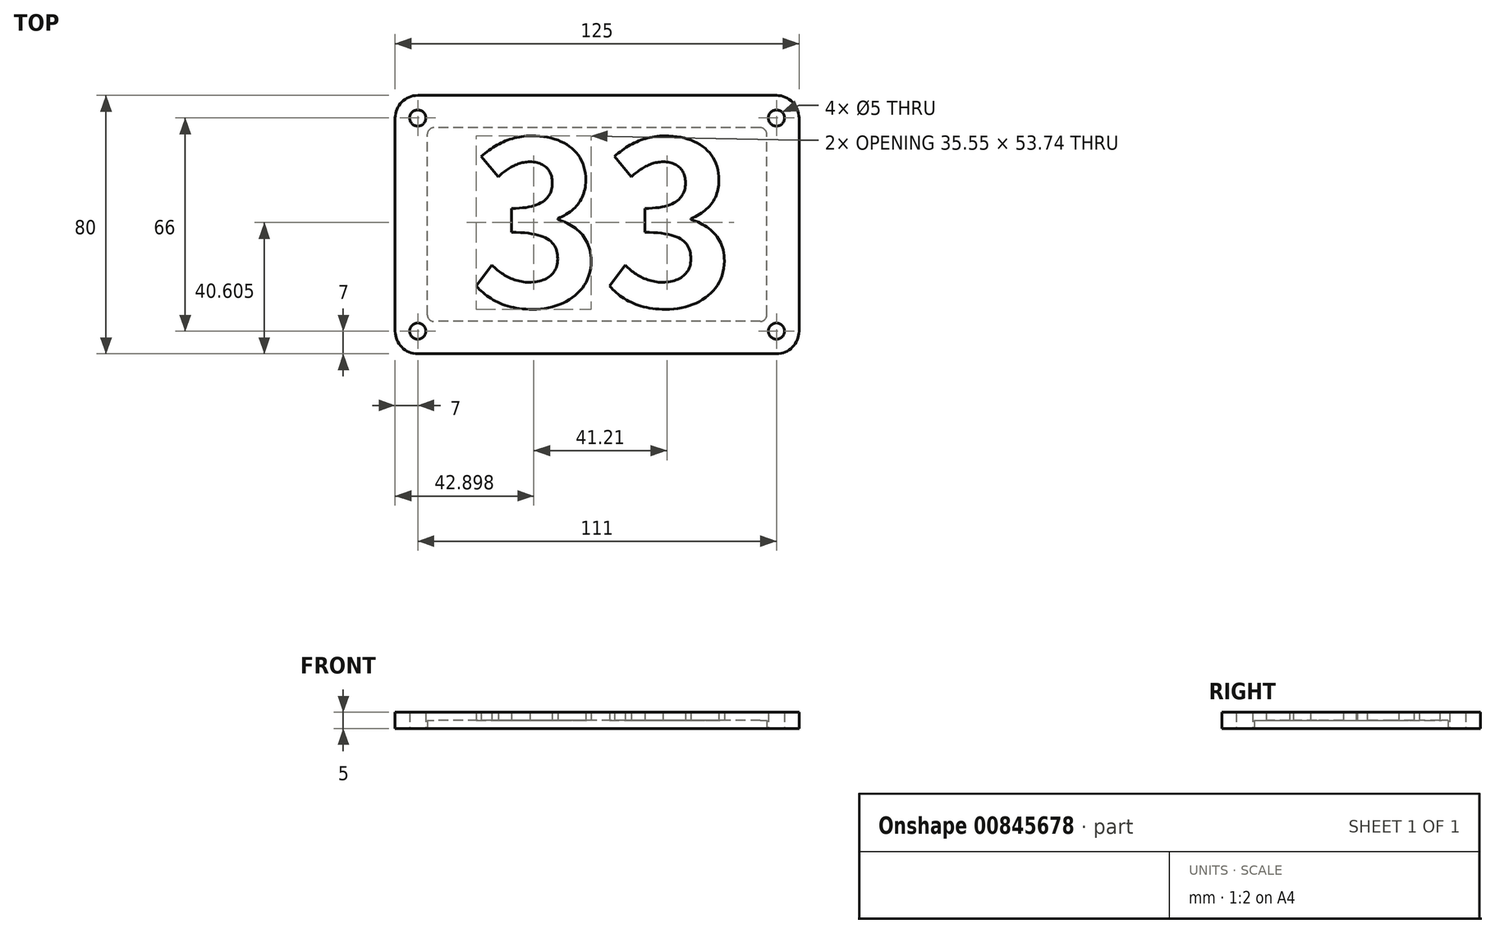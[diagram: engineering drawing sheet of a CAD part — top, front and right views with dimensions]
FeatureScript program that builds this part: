
annotation { "Feature Type Name" : "Feature", "Feature Type Description" : "" }
export const myFeature = defineFeature(function(context is Context, id is Id, definition is map)
    precondition{}
    {
        {
            var Q0;
            Q0=qCreatedBy(makeId("Top.planeOp"),FACE);
            var sketch = newSketch(context, id + "F0", { "sketchPlane" : qUnion([Q0])});
            skLineSegment(sketch, "E0.bottom", {"start": v(55.5, -40) * mm, "end": v(-55.5, -40) * mm});
            skLineSegment(sketch, "E0.top", {"start": v(55.5, 40) * mm, "end": v(-55.5, 40) * mm});
            skLineSegment(sketch, "E0.left", {"start": v(62.5, -33) * mm, "end": v(62.5, 33) * mm});
            skLineSegment(sketch, "E0.right", {"start": v(-62.5, -33) * mm, "end": v(-62.5, 33) * mm});
            skPoint(sketch, "E0.middle", {"position": v(0, 0) * mm});
            skPoint(sketch, "E1.visualSharp", {"position": v(-62.5, 40) * mm});
            skArc(sketch, "E1.filletArc", {"start": v(-55.5, 40) * mm, "mid": v(-60.45, 37.95) * mm, "end": v(-62.5, 33) * mm});
            skPoint(sketch, "E2.visualSharp", {"position": v(62.5, 40) * mm});
            skArc(sketch, "E2.filletArc", {"start": v(62.5, 33) * mm, "mid": v(60.45, 37.95) * mm, "end": v(55.5, 40) * mm});
            skPoint(sketch, "E3.visualSharp", {"position": v(62.5, -40) * mm});
            skArc(sketch, "E3.filletArc", {"start": v(55.5, -40) * mm, "mid": v(60.45, -37.95) * mm, "end": v(62.5, -33) * mm});
            skPoint(sketch, "E4.visualSharp", {"position": v(-62.5, -40) * mm});
            skArc(sketch, "E4.filletArc", {"start": v(-62.5, -33) * mm, "mid": v(-60.45, -37.95) * mm, "end": v(-55.5, -40) * mm});
            skCircle(sketch, "E5", {"center": v(55.5, 33) * mm, "radius": 2.5 * mm});
            skCircle(sketch, "E6", {"center": v(55.5, -33) * mm, "radius": 2.5 * mm});
            skCircle(sketch, "E7", {"center": v(-55.5, -33) * mm, "radius": 2.5 * mm});
            skCircle(sketch, "E8", {"center": v(-55.5, 33) * mm, "radius": 2.5 * mm});
            skSolve(sketch);
        }
        {
            var Q0;
            Q0=makeQuery(id+"F0.imprint","IMPRINT",FACE,{"disambiguationData":[TD([[makeQuery(id+"F0.imprint","IMPRINT",EDGE,{"derivedFrom":sQuery(id+"F0.wireOp",EDGE,"E0.bottom")}),-1.0]])]});
            extrude(context, id + "F1", {"entities" : qUnion([Q0]), "depth" : 5 * mm, "offsetDistance" : 25 * mm});
        }
        {
            var Q0;
            Q0=qCreatedBy(makeId("Top.planeOp"),FACE);
            var sketch = newSketch(context, id + "F2", { "sketchPlane" : qUnion([Q0])});
            skLineSegment(sketch, "E9.bottom", {"start": v(50.5, -30) * mm, "end": v(-50.5, -30) * mm});
            skLineSegment(sketch, "E9.top", {"start": v(50.5, 30) * mm, "end": v(-50.5, 30) * mm});
            skLineSegment(sketch, "E9.left", {"start": v(52.5, -28) * mm, "end": v(52.5, 28) * mm});
            skLineSegment(sketch, "E9.right", {"start": v(-52.5, -28) * mm, "end": v(-52.5, 28) * mm});
            skPoint(sketch, "E9.middle", {"position": v(0, 0) * mm});
            skPoint(sketch, "E10.visualSharp", {"position": v(-52.5, 30) * mm});
            skArc(sketch, "E10.filletArc", {"start": v(-50.5, 30) * mm, "mid": v(-51.91, 29.41) * mm, "end": v(-52.5, 28) * mm});
            skPoint(sketch, "E11.visualSharp", {"position": v(52.5, 30) * mm});
            skArc(sketch, "E11.filletArc", {"start": v(52.5, 28) * mm, "mid": v(51.91, 29.41) * mm, "end": v(50.5, 30) * mm});
            skPoint(sketch, "E12.visualSharp", {"position": v(52.5, -30) * mm});
            skArc(sketch, "E12.filletArc", {"start": v(50.5, -30) * mm, "mid": v(51.91, -29.41) * mm, "end": v(52.5, -28) * mm});
            skPoint(sketch, "E13.visualSharp", {"position": v(-52.5, -30) * mm});
            skArc(sketch, "E13.filletArc", {"start": v(-52.5, -28) * mm, "mid": v(-51.91, -29.41) * mm, "end": v(-50.5, -30) * mm});
            skSolve(sketch);
        }
        {
            var Q0;
            Q0=makeQuery(id+"F2.imprint","IMPRINT",FACE,{"disambiguationData":[TD([[makeQuery(id+"F2.imprint","IMPRINT",EDGE,{"derivedFrom":sQuery(id+"F2.wireOp",EDGE,"E9.bottom")}),-1.0]])]});
            extrude(context, id + "F3", {"entities" : qUnion([Q0]), "operationType" : NewBodyOperationType.REMOVE, "depth" : 2.5 * mm, "offsetDistance" : 25 * mm});
        }
        {
            var Q0;
            Q0=qCreatedBy(makeId("Top.planeOp"),FACE);
            var sketch = newSketch(context, id + "F4", { "sketchPlane" : qUnion([Q0])});
            skText(sketch, "E14", { "text": "33", "fontName": "NotoSansCJKjp-Bold.otf"});
            const initialGuessF4  = {"E14": [-0.03919, -0.02528, 1, 0, 0.05037]};
            skSetInitialGuess(sketch, initialGuessF4);
            skSolve(sketch);
        }
        {
            var Q0;
            Q0 = qSketchRegion(id + "F4", true);
            extrude(context, id + "F5", {"entities" : qUnion([Q0]), "operationType" : NewBodyOperationType.REMOVE, "endBound" : BoundingType.THROUGH_ALL, "depth" : 25 * mm, "offsetDistance" : 25 * mm});
        }
    });
